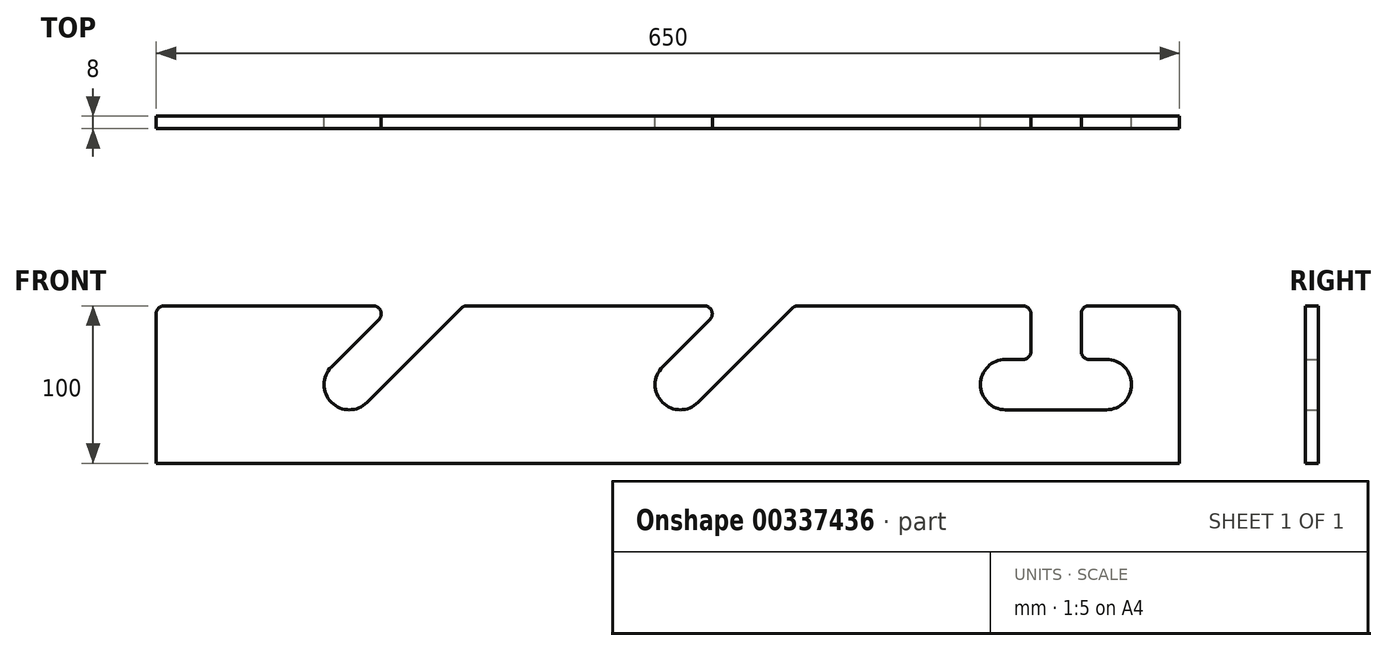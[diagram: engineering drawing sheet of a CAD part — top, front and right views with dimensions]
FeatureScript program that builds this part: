
annotation { "Feature Type Name" : "Feature", "Feature Type Description" : "" }
export const myFeature = defineFeature(function(context is Context, id is Id, definition is map)
    precondition{}
    {
        {
            var Q0;
            Q0=qCreatedBy(makeId("Front.planeOp"),FACE);
            var sketch = newSketch(context, id + "F0", { "sketchPlane" : qUnion([Q0])});
            skLineSegment(sketch, "E0.bottom", {"start": v(-85.06, 50) * mm, "end": v(47.87, 50) * mm});
            skLineSegment(sketch, "E0.top", {"start": v(-90.06, -50) * mm, "end": v(559.94, -50) * mm});
            skLineSegment(sketch, "E0.left", {"start": v(-90.06, 45) * mm, "end": v(-90.06, -50) * mm});
            skLineSegment(sketch, "E0.right", {"start": v(559.94, 45) * mm, "end": v(559.94, -50) * mm});
            skArc(sketch, "E1", {"start": v(21.25, 11.31) * mm, "mid": v(21.25, -11.31) * mm, "end": v(43.88, -11.31) * mm});
            skArc(sketch, "E2", {"start": v(231.5, 11.31) * mm, "mid": v(231.5, -11.31) * mm, "end": v(254.14, -11.31) * mm});
            skArc(sketch, "E3", {"start": v(449.45, 16) * mm, "mid": v(433.45, 0) * mm, "end": v(449.45, -16) * mm});
            skArc(sketch, "E4", {"start": v(513.45, -16) * mm, "mid": v(529.45, 0) * mm, "end": v(513.45, 16) * mm});
            skLineSegment(sketch, "E5", {"start": v(21.25, 11.31) * mm, "end": v(51.4, 41.46) * mm});
            skLineSegment(sketch, "E6", {"start": v(103.73, 48.54) * mm, "end": v(43.88, -11.31) * mm});
            skLineSegment(sketch, "E7", {"start": v(231.5, 11.31) * mm, "end": v(261.66, 41.46) * mm});
            skLineSegment(sketch, "E8", {"start": v(254.14, -11.31) * mm, "end": v(313.98, 48.54) * mm});
            skLineSegment(sketch, "E9.trimOffspring", {"start": v(107.27, 50) * mm, "end": v(258.12, 50) * mm});
            skLineSegment(sketch, "E10.trimOffspring", {"start": v(317.52, 50) * mm, "end": v(460.45, 50) * mm});
            skLineSegment(sketch, "E11", {"start": v(465.45, 21) * mm, "end": v(465.45, 45) * mm});
            skLineSegment(sketch, "E12", {"start": v(497.45, 21) * mm, "end": v(497.45, 45) * mm});
            skLineSegment(sketch, "E13", {"start": v(449.45, -16) * mm, "end": v(513.45, -16) * mm});
            skLineSegment(sketch, "E14", {"start": v(449.45, 16) * mm, "end": v(460.45, 16) * mm});
            skPoint(sketch, "E15.orphan", {"position": v(465.45, 0) * mm});
            skPoint(sketch, "E16.orphan", {"position": v(497.45, 0) * mm});
            skLineSegment(sketch, "E17.trimOffspring", {"start": v(502.45, 16) * mm, "end": v(513.45, 16) * mm});
            skLineSegment(sketch, "E18.trimOffspring", {"start": v(502.45, 50) * mm, "end": v(554.94, 50) * mm});
            skPoint(sketch, "E19.visualSharp", {"position": v(559.94, 50) * mm});
            skArc(sketch, "E19.filletArc", {"start": v(559.94, 45) * mm, "mid": v(558.48, 48.54) * mm, "end": v(554.94, 50) * mm});
            skPoint(sketch, "E20.visualSharp", {"position": v(497.45, 50) * mm});
            skArc(sketch, "E20.filletArc", {"start": v(502.45, 50) * mm, "mid": v(498.91, 48.54) * mm, "end": v(497.45, 45) * mm});
            skPoint(sketch, "E21.visualSharp", {"position": v(497.45, 16) * mm});
            skArc(sketch, "E21.filletArc", {"start": v(497.45, 21) * mm, "mid": v(498.91, 17.46) * mm, "end": v(502.45, 16) * mm});
            skPoint(sketch, "E22.visualSharp", {"position": v(465.45, 16) * mm});
            skArc(sketch, "E22.filletArc", {"start": v(460.45, 16) * mm, "mid": v(463.98, 17.46) * mm, "end": v(465.45, 21) * mm});
            skPoint(sketch, "E23.visualSharp", {"position": v(465.45, 50) * mm});
            skArc(sketch, "E23.filletArc", {"start": v(465.45, 45) * mm, "mid": v(463.98, 48.54) * mm, "end": v(460.45, 50) * mm});
            skPoint(sketch, "E24.visualSharp", {"position": v(315.45, 50) * mm});
            skArc(sketch, "E24.filletArc", {"start": v(317.52, 50) * mm, "mid": v(315.6, 49.62) * mm, "end": v(313.98, 48.54) * mm});
            skPoint(sketch, "E25.visualSharp", {"position": v(270.2, 50) * mm});
            skArc(sketch, "E25.filletArc", {"start": v(261.66, 41.46) * mm, "mid": v(262.74, 46.91) * mm, "end": v(258.12, 50) * mm});
            skPoint(sketch, "E26.visualSharp", {"position": v(105.2, 50) * mm});
            skArc(sketch, "E26.filletArc", {"start": v(107.27, 50) * mm, "mid": v(105.35, 49.62) * mm, "end": v(103.73, 48.54) * mm});
            skPoint(sketch, "E27.visualSharp", {"position": v(59.94, 50) * mm});
            skArc(sketch, "E27.filletArc", {"start": v(51.4, 41.46) * mm, "mid": v(52.49, 46.91) * mm, "end": v(47.87, 50) * mm});
            skPoint(sketch, "E28.visualSharp", {"position": v(-90.06, 50) * mm});
            skArc(sketch, "E28.filletArc", {"start": v(-85.06, 50) * mm, "mid": v(-88.6, 48.54) * mm, "end": v(-90.06, 45) * mm});
            skSolve(sketch);
        }
        {
            var Q0;
            Q0 = qSketchRegion(id + "F0", true);
            extrude(context, id + "F1", {"entities" : qUnion([Q0]), "depth" : 8 * mm});
        }
    });
